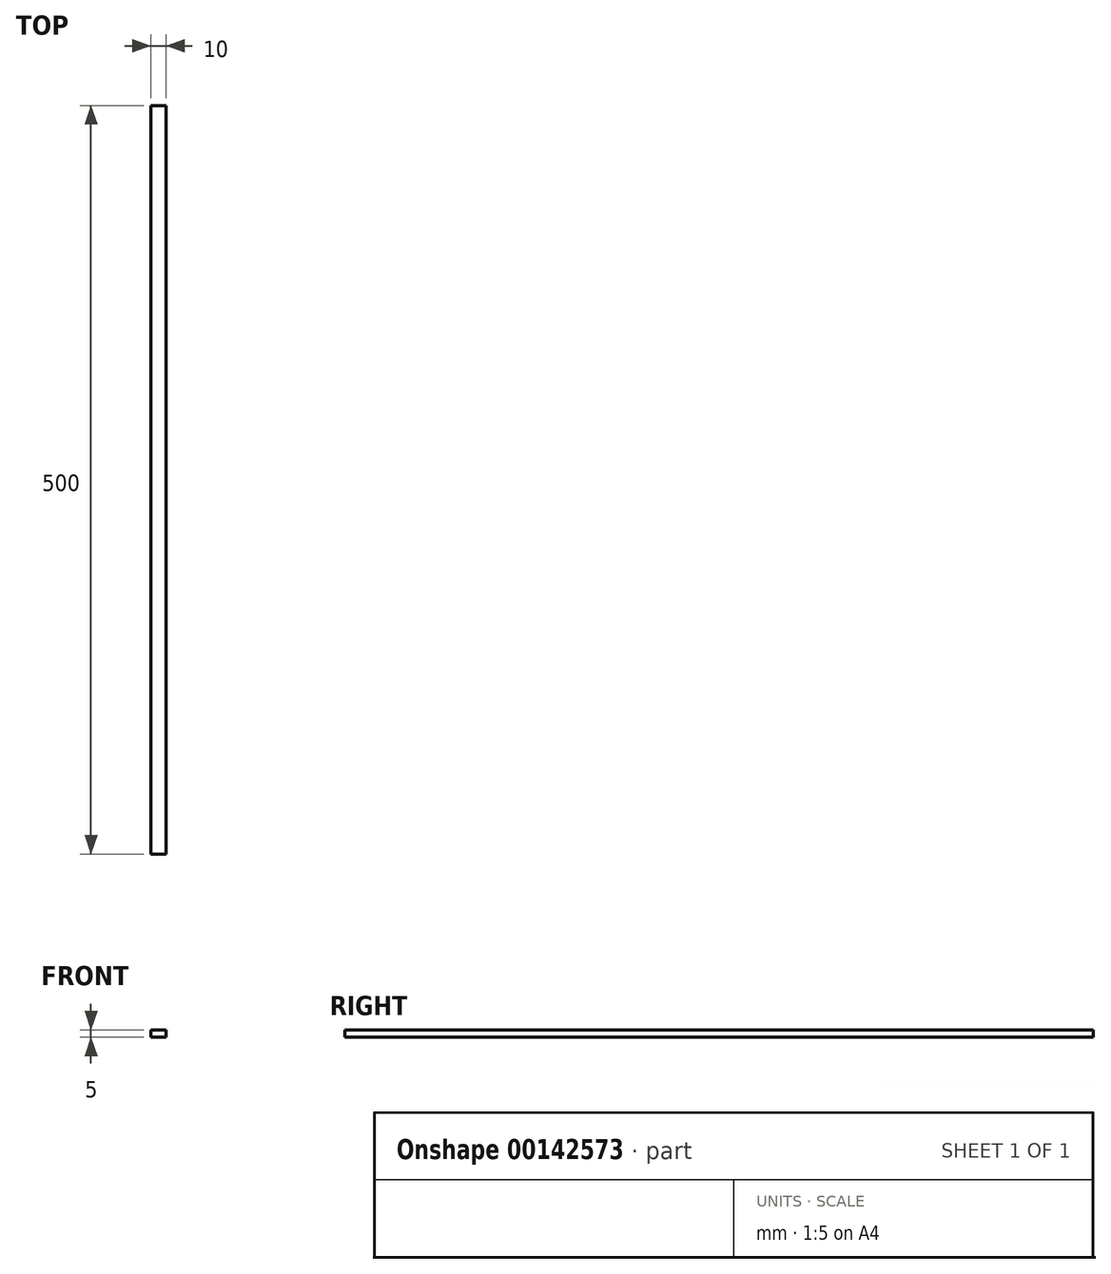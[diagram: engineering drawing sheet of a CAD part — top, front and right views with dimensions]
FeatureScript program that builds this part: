
annotation { "Feature Type Name" : "Feature", "Feature Type Description" : "" }
export const myFeature = defineFeature(function(context is Context, id is Id, definition is map)
    precondition{}
    {
        {
            var Q0;
            Q0=qCreatedBy(makeId("Front.planeOp"),FACE);
            var sketch = newSketch(context, id + "F0", { "sketchPlane" : qUnion([Q0])});
            skLineSegment(sketch, "E0.bottom", {"start": v(5, 2.5) * mm, "end": v(-5, 2.5) * mm});
            skLineSegment(sketch, "E0.top", {"start": v(5, -2.5) * mm, "end": v(-5, -2.5) * mm});
            skLineSegment(sketch, "E0.left", {"start": v(5, 2.5) * mm, "end": v(5, -2.5) * mm});
            skLineSegment(sketch, "E0.right", {"start": v(-5, 2.5) * mm, "end": v(-5, -2.5) * mm});
            skPoint(sketch, "E0.middle", {"position": v(0, 0) * mm});
            skSolve(sketch);
        }
        {
            var Q0;
            Q0=makeQuery(id+"F0.imprint","IMPRINT",FACE,{"disambiguationData":[TD([[makeQuery(id+"F0.imprint","IMPRINT",EDGE,{"derivedFrom":sQuery(id+"F0.wireOp",EDGE,"E0.bottom")}),1.0]])]});
            extrude(context, id + "F1", {"entities" : qUnion([Q0]), "oppositeDirection" : true, "depth" : 500 * mm});
        }
    });
